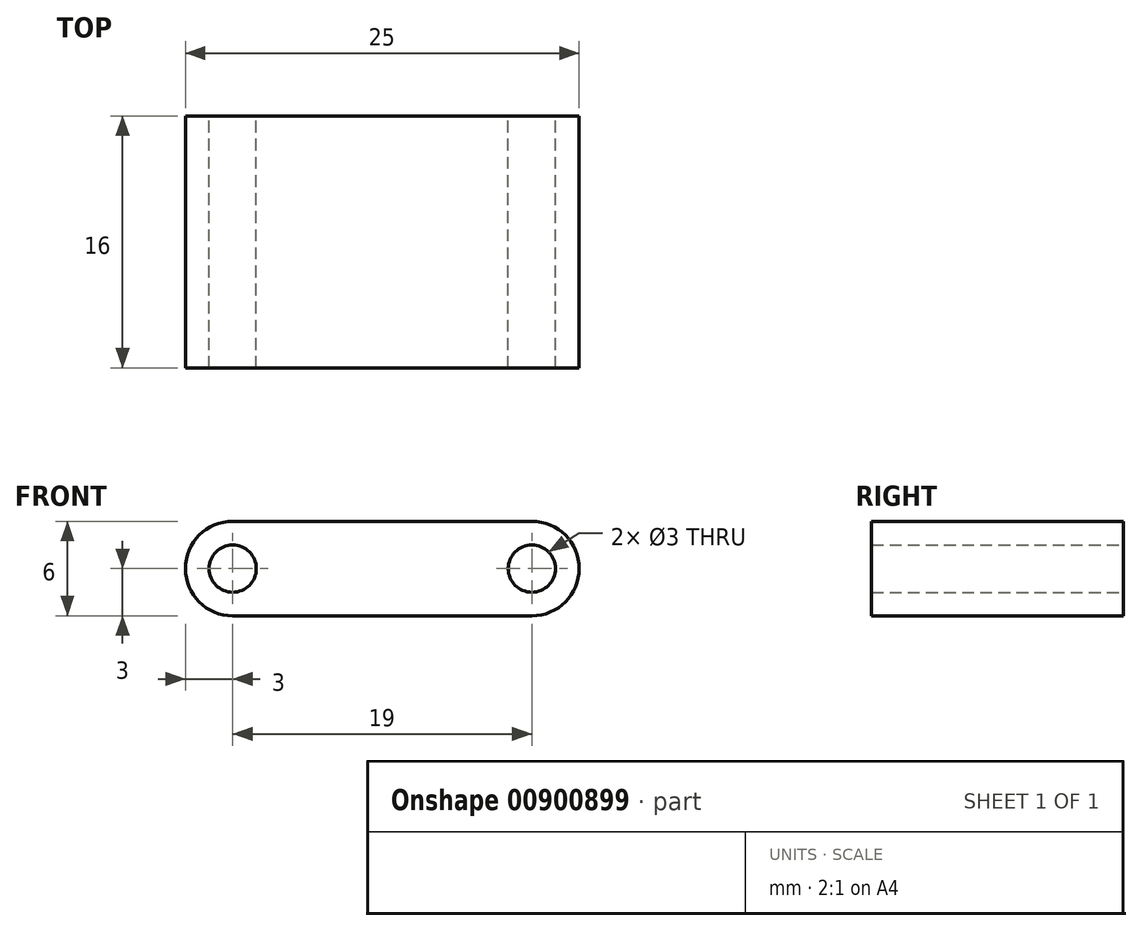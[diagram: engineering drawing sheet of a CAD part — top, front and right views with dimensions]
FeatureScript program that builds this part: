
annotation { "Feature Type Name" : "Feature", "Feature Type Description" : "" }
export const myFeature = defineFeature(function(context is Context, id is Id, definition is map)
    precondition{}
    {
        {
            var Q0;
            Q0=qCreatedBy(makeId("Front.planeOp"),FACE);
            var sketch = newSketch(context, id + "F0", { "sketchPlane" : qUnion([Q0])});
            skArc(sketch, "E0", {"start": v(-9.85, 3) * mm, "mid": v(-12.85, 0) * mm, "end": v(-9.85, -3) * mm});
            skCircle(sketch, "E1", {"center": v(-9.85, 0) * mm, "radius": 1.5 * mm});
            skArc(sketch, "E2", {"start": v(9.15, -3) * mm, "mid": v(12.15, 0) * mm, "end": v(9.15, 3) * mm});
            skCircle(sketch, "E3", {"center": v(9.15, 0) * mm, "radius": 1.5 * mm});
            skLineSegment(sketch, "E4", {"start": v(-9.85, 3) * mm, "end": v(9.15, 3) * mm});
            skLineSegment(sketch, "E5", {"start": v(-9.85, -3) * mm, "end": v(9.15, -3) * mm});
            skSolve(sketch);
        }
        {
            var Q0;
            Q0 = qSketchRegion(id + "F0", true);
            extrude(context, id + "F1", {"entities" : qUnion([Q0]), "endBound" : BoundingType.SYMMETRIC, "depth" : 16 * mm, "offsetDistance" : 25 * mm});
        }
    });
